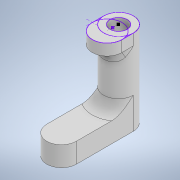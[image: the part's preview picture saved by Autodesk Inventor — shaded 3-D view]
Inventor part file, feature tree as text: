
AUTODESK INVENTOR PART (.ipt)
format: ipt  version: 2021.1 (Build 251245010, 245A)  size: 234,496 bytes
history: native  units: mm
features: extrude x3, other x2, sketch x2, fillet x2
ambient origin geometry x8: Origin, YZ Plane, XZ Plane, XY Plane, X Axis, Y Axis, Z Axis, Center Point
bodies: Volumenkörper1 (feature_tree)
feature tree (9):
  other  "OBS-M-003_v4"
  sketch  "Skizze1"  dims[d0=2.0mm d1=0.0mm d2=11.5mm d3=0.0mm]
  extrude  "Extrusion1"  Depth=2.0mm TaperAngle=0.0deg
  extrude  "Extrusion2"  Depth=2.0mm TaperAngle=0.0deg
  fillet  "Rundung1"  Radius=2.0mm
  extrude  "Extrusion3"  [1 undecoded]
  fillet  "Rundung2"  [1 undecoded]
  sketch  "Skizze2"  dims[d4=2.0mm d6=3.5mm d7=0.0mm d8=2.0mm]
  other  "MeshFeature1"
note: 2 required parameter values undecoded (feature->parameter linkage not recoverable at this tier; creation-order binding heuristic only, values carry confidence <= 0.55)
